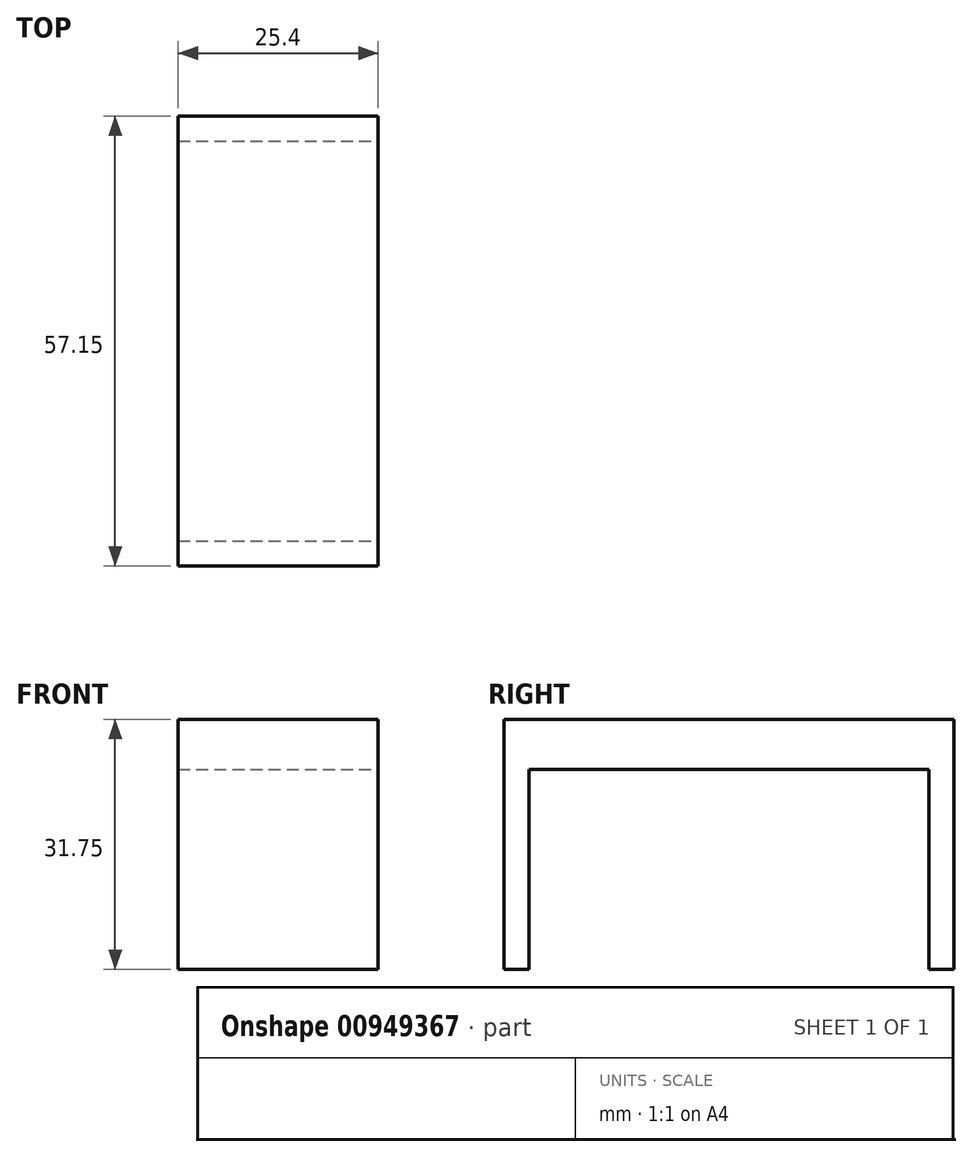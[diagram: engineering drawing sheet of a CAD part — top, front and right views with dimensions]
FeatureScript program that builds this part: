
annotation { "Feature Type Name" : "Feature", "Feature Type Description" : "" }
export const myFeature = defineFeature(function(context is Context, id is Id, definition is map)
    precondition{}
    {
        {
            var Q0;
            Q0=qCreatedBy(makeId("Top.planeOp"),FACE);
            var sketch = newSketch(context, id + "F0", { "sketchPlane" : qUnion([Q0])});
            skLineSegment(sketch, "E0.bottom", {"start": v(-29.33, 22.12) * mm, "end": v(-3.93, 22.12) * mm});
            skLineSegment(sketch, "E0.top", {"start": v(-29.33, -28.68) * mm, "end": v(-3.93, -28.68) * mm});
            skLineSegment(sketch, "E0.left", {"start": v(-29.33, 22.12) * mm, "end": v(-29.33, -28.68) * mm});
            skLineSegment(sketch, "E0.right", {"start": v(-3.93, 22.12) * mm, "end": v(-3.93, -28.68) * mm});
            skLineSegment(sketch, "E1.bottom", {"start": v(-29.33, 25.3) * mm, "end": v(-3.93, 25.3) * mm});
            skLineSegment(sketch, "E1.top", {"start": v(-29.33, -31.86) * mm, "end": v(-3.93, -31.86) * mm});
            skLineSegment(sketch, "E1.left", {"start": v(-29.33, 25.3) * mm, "end": v(-29.33, -31.86) * mm});
            skLineSegment(sketch, "E1.right", {"start": v(-3.93, 25.3) * mm, "end": v(-3.93, -31.86) * mm});
            skSolve(sketch);
        }
        {
            var Q0;
            {var subQ0=sQuery(id+"F0.wireOp",EDGE,"E0.bottom");Q0=makeQuery(id+"F0.imprint","IMPRINT",FACE,{"disambiguationData":[TD([[makeQuery(id+"F0.imprint","IMPRINT",EDGE,{"derivedFrom":subQ0}),1.0]])]});}
            var Q1;
            {var subQ0=sQuery(id+"F0.wireOp",EDGE,"E0.bottom");Q1=makeQuery(id+"F0.imprint","IMPRINT",FACE,{"disambiguationData":[TD([[makeQuery(id+"F0.imprint","IMPRINT",EDGE,{"derivedFrom":subQ0}),-1.0]])]});}
            var Q2;
            {var subQ0=sQuery(id+"F0.wireOp",EDGE,"E0.top");Q2=makeQuery(id+"F0.imprint","IMPRINT",FACE,{"disambiguationData":[TD([[makeQuery(id+"F0.imprint","IMPRINT",EDGE,{"derivedFrom":subQ0}),-1.0]])]});}
            extrude(context, id + "F1", {"entities" : qUnion([Q0, Q1, Q2]), "depth" : 31.75 * mm, "offsetDistance" : 25.4 * mm});
        }
        {
            var Q0;
            {var subQ0=sQuery(id+"F0.wireOp",EDGE,"E0.bottom");Q0=makeQuery(id+"F0.imprint","IMPRINT",FACE,{"disambiguationData":[TD([[makeQuery(id+"F0.imprint","IMPRINT",EDGE,{"derivedFrom":subQ0}),-1.0]])]});}
            extrude(context, id + "F2", {"entities" : qUnion([Q0]), "operationType" : NewBodyOperationType.REMOVE, "depth" : 25.4 * mm, "offsetDistance" : 25.4 * mm});
        }
    });
